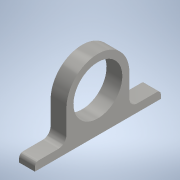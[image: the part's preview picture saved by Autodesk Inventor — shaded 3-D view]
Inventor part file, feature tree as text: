
AUTODESK INVENTOR PART (.ipt)
format: ipt  version: 2022.1 (Build 261234000, 234)  size: 107,520 bytes
history: native  units: mm (DEFAULTED — no unit token found)
features: other x7, extrude x1, sketch x1
bodies: Body1 (feature_tree)
feature tree (9):
  other  "Origen"
  extrude  "Extrusión3"  Depth=80.0mm
  other  "Plano YZ"
  other  "Plano XZ"
  other  "Plano XY"
  other  "Eje X"
  other  "Eje Y"
  other  "Eje Z"
  sketch  "Boceto3"  dims[d26=62.0mm d27=80.0mm d28=160.0mm d29=49.5mm d30=10.0mm d31=5.0mm d32=5.0mm d33=10.0mm d34=20.0mm d35=0.0mm d25=0.5mm]
